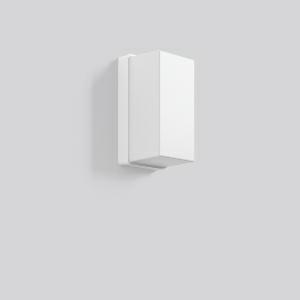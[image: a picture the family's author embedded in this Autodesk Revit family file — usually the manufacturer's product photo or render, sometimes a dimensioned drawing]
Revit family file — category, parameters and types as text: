
# Revit family: rechteck_22144_002_9aed
name_source: partatom
category: Lighting Fixtures
units: mm (PartAtom-declared; Revit-internal decimal feet)

## family parameters
Cut with Voids When Loaded = No
Host = Face
Light Source = No
Part Type = Normal
Room Calculation Point = No
Round Connector Dimension = Use Diameter
Shared = No

## types (1)
- RECHTECK (1 x QA60/clear E27, 700 lm, 46 W, 3000)
    Apparent Load = 46 VA
    CIE Flux Codes = 35 64 85 77 54
    Color Rendering = 90
    Color Temperature = 3000
    Default Elevation = 1800 mm
    Description = Series: RECHTECK
Rectangular surface-mounted luminaire in classic design. Base: plastic. Diffuser: plastic (polypropylene), opal, satin finish. Diffuser fastening: spring system. Suitable for Wall (surface). 
Colour: white
Length: 215 mm
Width: 115 mm
Height: 110 mm
Lamp: A60
Number of lamps: 1
Wattage: 60 W
Socket: E27
System power: 17 W
Rated luminous flux: 490 lm
Luminous efficiency: 29 lm/W
Control gear: Converter not necessary
Protection class: II
Type of protection: IP 44
    Height = 110 mm
    Lamp = 1 x QA60/clear E27
    Lamp Light Flux = 700 lm
    Lamp Power = 46 W
    Lamp count = 1
    Length = 215 mm
    Lifetime = 3000 h
    Luminous efficacy = 8 lm/W
    Manufacturer = RZB
    ModVariant = No
    Model = 22144.002
    Mounting Place = Wall, Ceiling
    Mounting Type = Surface mounted
    Number of Poles = 1
    OnlyDefault = Yes
    Power Factor = 1
    Product Name = RECHTECK
    Product group = Surface mounted ceiling and wall luminaires
    ProductGroupID = 305
    Protection Class = Protection class II
    Protection Degree = IP 44
    RLX_Detail_Level = 1
    RLX_Emergency_Light_Flux = 0 lm
    RLX_Emergency_Type = 0
    RLX_Emergency_Type_DB = No
    RlxData = <blob elided: 12849 chars, md5=79f48c2e>
    Socket = E27
    Standby Power = 0 W
    System Light Flux = 379 lm
    System Power = 46 W
    Type Comments = Product without accessories
    Type Image = 22144.002.jpg
    URL = http://relux.com
    VarID = ---
    Voltage = 230 V
    Voltage Range = 220-240 V
    Weight = 0.00 kg
    Width = 115 mm

## geometry (parser evidence)
native form markers: Sweep x11
no freeform markers — native parametric forms only
